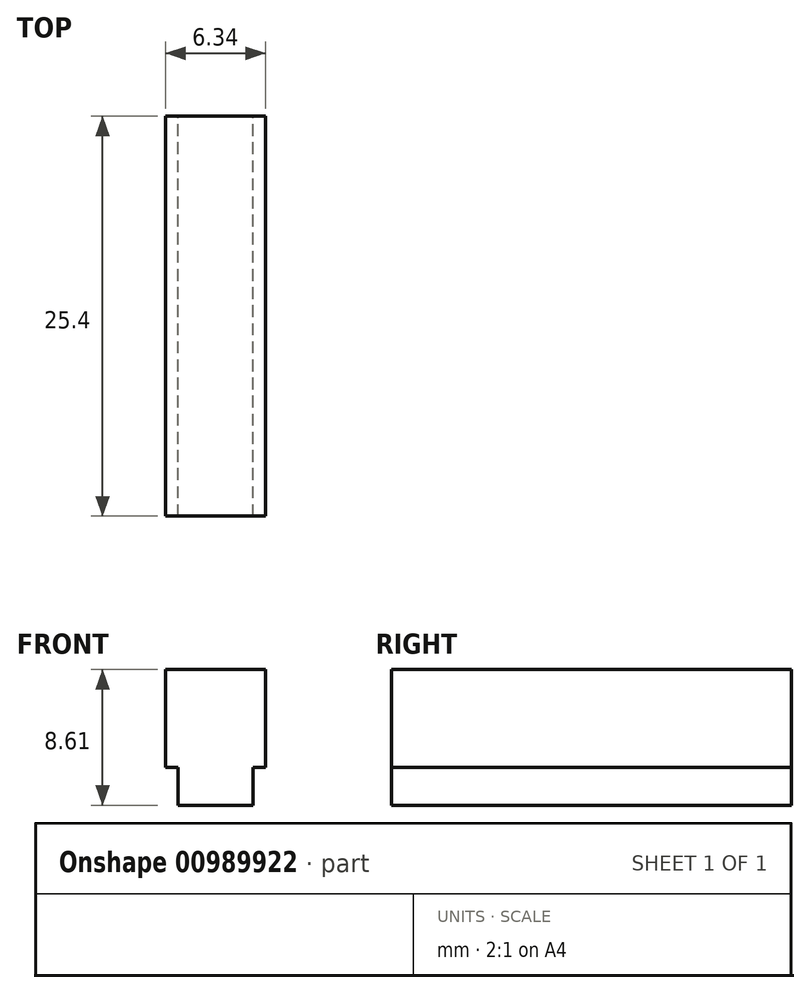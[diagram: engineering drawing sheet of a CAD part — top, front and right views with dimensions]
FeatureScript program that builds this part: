
annotation { "Feature Type Name" : "Feature", "Feature Type Description" : "" }
export const myFeature = defineFeature(function(context is Context, id is Id, definition is map)
    precondition{}
    {
        {
            var Q0;
            Q0=qCreatedBy(makeId("Front.planeOp"),FACE);
            var sketch = newSketch(context, id + "F0", { "sketchPlane" : qUnion([Q0])});
            skLineSegment(sketch, "E0", {"start": v(-2.38, 0) * mm, "end": v(2.38, 0) * mm});
            skLineSegment(sketch, "E1", {"start": v(2.38, 0) * mm, "end": v(2.38, 2.39) * mm});
            skLineSegment(sketch, "E2", {"start": v(2.38, 2.39) * mm, "end": v(3.18, 2.39) * mm});
            skLineSegment(sketch, "E3", {"start": v(3.18, 2.39) * mm, "end": v(3.18, 8.61) * mm});
            skLineSegment(sketch, "E4", {"start": v(3.17, 8.61) * mm, "end": v(-3.17, 8.61) * mm});
            skLineSegment(sketch, "E5", {"start": v(-2.38, 0) * mm, "end": v(-2.38, 2.39) * mm});
            skLineSegment(sketch, "E6", {"start": v(-2.38, 2.39) * mm, "end": v(-3.18, 2.39) * mm});
            skLineSegment(sketch, "E7", {"start": v(-3.18, 2.39) * mm, "end": v(-3.18, 8.61) * mm});
            skCircle(sketch, "E8", {"center": v(0, -6.83) * mm, "radius": 9.53 * mm, "construction": true});
            skCircle(sketch, "E9", {"center": v(0, -6.83) * mm, "radius": 12.7 * mm, "construction": true});
            skPoint(sketch, "E10", {"position": v(0, 5.87) * mm});
            skPoint(sketch, "E11", {"position": v(0, 2.7) * mm});
            skSolve(sketch);
        }
        {
            var Q0;
            Q0=makeQuery(id+"F0.imprint","IMPRINT",FACE,{"disambiguationData":[TD([[makeQuery(id+"F0.imprint","IMPRINT",EDGE,{"derivedFrom":sQuery(id+"F0.wireOp",EDGE,"E0")}),1.0]])]});
            extrude(context, id + "F1", {"entities" : qUnion([Q0]), "endBound" : BoundingType.SYMMETRIC, "depth" : 25.4 * mm, "offsetDistance" : 25.4 * mm});
        }
    });
